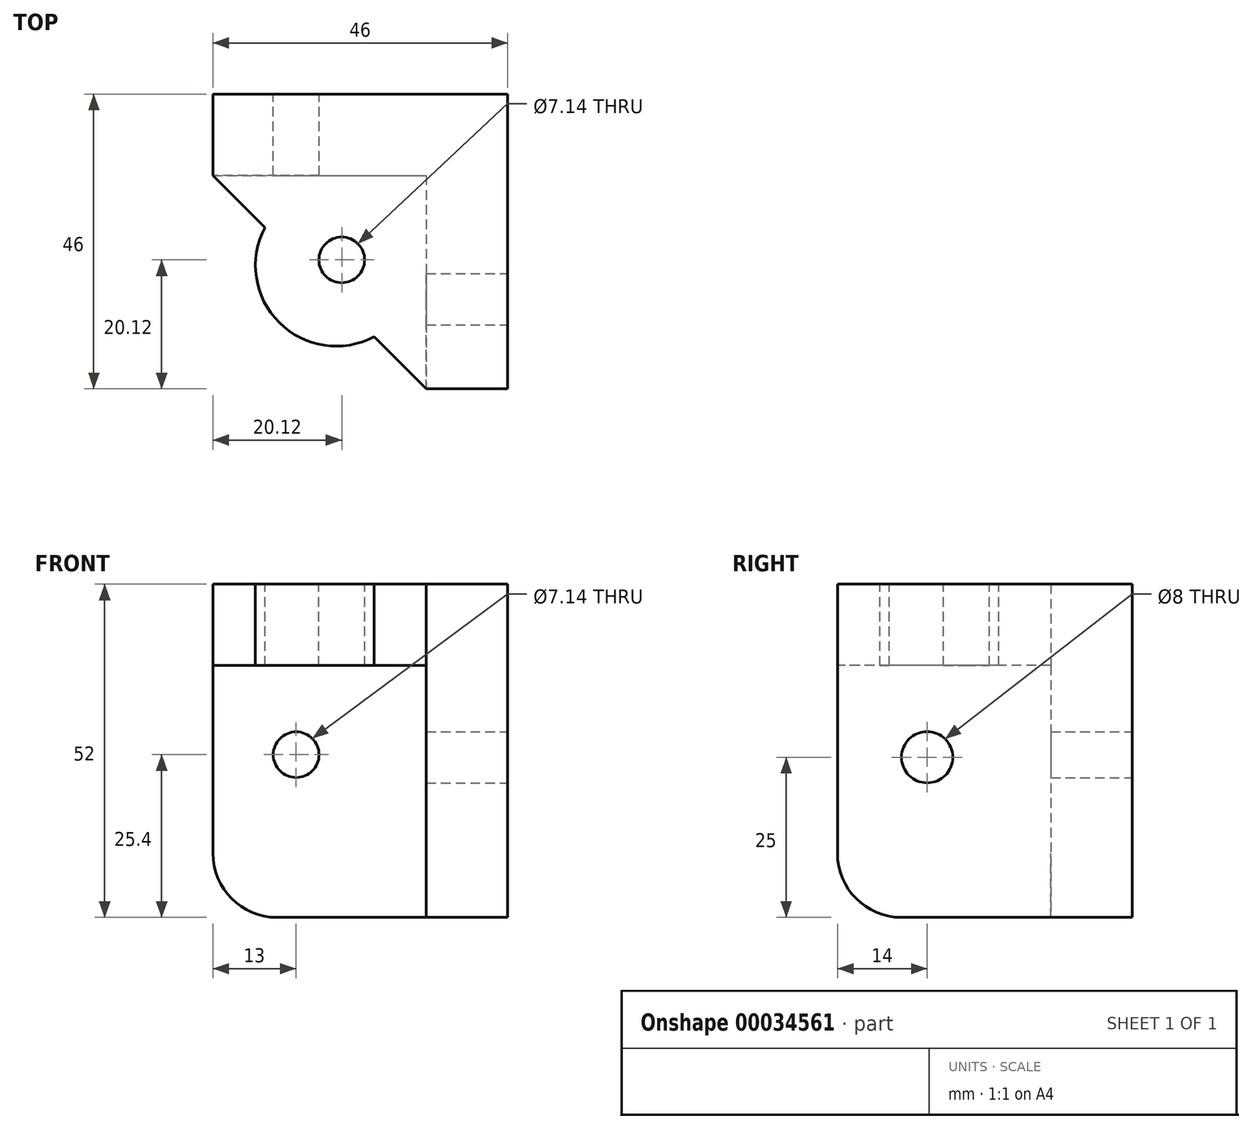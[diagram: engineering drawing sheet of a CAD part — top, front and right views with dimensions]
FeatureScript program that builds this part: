
annotation { "Feature Type Name" : "Feature", "Feature Type Description" : "" }
export const myFeature = defineFeature(function(context is Context, id is Id, definition is map)
    precondition{}
    {
        {
            var Q0;
            Q0=qCreatedBy(makeId("Top.planeOp"),FACE);
            var sketch = newSketch(context, id + "F0", { "sketchPlane" : qUnion([Q0])});
            skLineSegment(sketch, "E0.bottom", {"start": v(0, 0) * mm, "end": v(33.3, 0) * mm});
            skLineSegment(sketch, "E0.top", {"start": v(0, -12.7) * mm, "end": v(33.3, -12.7) * mm});
            skLineSegment(sketch, "E0.left", {"start": v(0, 0) * mm, "end": v(0, -12.7) * mm});
            skLineSegment(sketch, "E0.right", {"start": v(33.3, 0) * mm, "end": v(33.3, -12.7) * mm});
            skLineSegment(sketch, "E1.bottom", {"start": v(33.3, 0) * mm, "end": v(46, 0) * mm});
            skLineSegment(sketch, "E1.top", {"start": v(33.3, -46) * mm, "end": v(46, -46) * mm});
            skLineSegment(sketch, "E1.left", {"start": v(33.3, 0) * mm, "end": v(33.3, -46) * mm});
            skLineSegment(sketch, "E1.right", {"start": v(46, 0) * mm, "end": v(46, -46) * mm});
            skSolve(sketch);
        }
        {
            var Q0;
            Q0 = qSketchRegion(id + "F0", true);
            extrude(context, id + "F1", {"entities" : qUnion([Q0]), "depth" : 52 * mm});
        }
        {
            var Q0;
            Q0=makeQuery(id+"F1.opExtrude","CAP_FACE",FACE,{"disambiguationData":[OSD([sQuery(id+"F0.wireOp",EDGE,"E0.bottom"),sQuery(id+"F0.wireOp",EDGE,"E0.top"),sQuery(id+"F0.wireOp",EDGE,"E0.left"),sQuery(id+"F0.wireOp",EDGE,"E1.bottom"),sQuery(id+"F0.wireOp",EDGE,"E1.top"),sQuery(id+"F0.wireOp",EDGE,"E1.left"),sQuery(id+"F0.wireOp",EDGE,"E1.right")])],"isStart":false});
            var sketch = newSketch(context, id + "F2", { "sketchPlane" : qUnion([Q0])});
            skLineSegment(sketch, "E2.bottom", {"start": v(46, 0) * mm, "end": v(0, 0) * mm});
            skLineSegment(sketch, "E2.top", {"start": v(46, -46) * mm, "end": v(0, -46) * mm, "construction": true});
            skLineSegment(sketch, "E2.left", {"start": v(46, 0) * mm, "end": v(46, -46) * mm});
            skLineSegment(sketch, "E2.right", {"start": v(0, 0) * mm, "end": v(0, -46) * mm, "construction": true});
            skLineSegment(sketch, "E3", {"start": v(0, 0) * mm, "end": v(0, -12.7) * mm});
            skLineSegment(sketch, "E4", {"start": v(0, -12.7) * mm, "end": v(33.3, -46) * mm});
            skLineSegment(sketch, "E5", {"start": v(33.3, -46) * mm, "end": v(46, -46) * mm});
            skArc(sketch, "E6", {"start": v(8.13, -20.83) * mm, "mid": v(10.34, -35.66) * mm, "end": v(25.17, -37.87) * mm});
            skLineSegment(sketch, "E7", {"start": v(46, 0) * mm, "end": v(16.65, -29.35) * mm, "construction": true});
            skSolve(sketch);
        }
        {
            var Q0;
            Q0 = qSketchRegion(id + "F2", true);
            extrude(context, id + "F3", {"entities" : qUnion([Q0]), "operationType" : NewBodyOperationType.ADD, "oppositeDirection" : true, "depth" : 12.7 * mm});
        }
        {
            var Q0;
            Q0=makeQuery(id+"F1.opExtrude","SWEPT_FACE",FACE,{"disambiguationData":[OSD([sQuery(id+"F0.wireOp",EDGE,"E1.right")])]});
            var sketch = newSketch(context, id + "F4", { "sketchPlane" : qUnion([Q0])});
            skCircle(sketch, "E8", {"center": v(-32, 25) * mm, "radius": 4 * mm});
            skPoint(sketch, "E8.centerSnap0", {"position": v(-32, 0) * mm});
            skSolve(sketch);
        }
        {
            var Q0;
            Q0 = qSketchRegion(id + "F4", true);
            extrude(context, id + "F5", {"entities" : qUnion([Q0]), "operationType" : NewBodyOperationType.REMOVE, "endBound" : BoundingType.THROUGH_ALL, "oppositeDirection" : true, "depth" : 25 * mm});
        }
        {
            var Q0;
            Q0=makeQuery(id+"F1.opExtrude","SWEPT_FACE",FACE,{"disambiguationData":[OSD([sQuery(id+"F0.wireOp",EDGE,"E0.bottom"),sQuery(id+"F0.wireOp",EDGE,"E1.bottom")])]});
            var sketch = newSketch(context, id + "F6", { "sketchPlane" : qUnion([Q0])});
            skCircle(sketch, "E9", {"center": v(-13, 25.4) * mm, "radius": 3.57 * mm});
            skSolve(sketch);
        }
        {
            var Q0;
            Q0 = qSketchRegion(id + "F6", true);
            extrude(context, id + "F7", {"entities" : qUnion([Q0]), "operationType" : NewBodyOperationType.REMOVE, "oppositeDirection" : true, "depth" : 25 * mm});
        }
        {
            var Q0;
            Q0=makeQuery(id+"F3.boolean.opBoolean","MERGE",FACE,{"derivedFrom":[makeQuery(id+"F1.opExtrude","CAP_FACE",FACE,{"disambiguationData":[OSD([sQuery(id+"F0.wireOp",EDGE,"E0.bottom"),sQuery(id+"F0.wireOp",EDGE,"E0.top"),sQuery(id+"F0.wireOp",EDGE,"E0.left"),sQuery(id+"F0.wireOp",EDGE,"E1.bottom"),sQuery(id+"F0.wireOp",EDGE,"E1.top"),sQuery(id+"F0.wireOp",EDGE,"E1.left"),sQuery(id+"F0.wireOp",EDGE,"E1.right")])],"isStart":false}),makeQuery(id+"F3.opExtrude","CAP_FACE",FACE,{"disambiguationData":[OSD([sQuery(id+"F2.wireOp",EDGE,"E2.bottom"),sQuery(id+"F2.wireOp",EDGE,"E2.left"),sQuery(id+"F2.wireOp",EDGE,"E3"),sQuery(id+"F2.wireOp",EDGE,"E4"),sQuery(id+"F2.wireOp",EDGE,"E5"),sQuery(id+"F2.wireOp",EDGE,"E6")])],"isStart":true})]});
            var sketch = newSketch(context, id + "F8", { "sketchPlane" : qUnion([Q0])});
            skCircle(sketch, "E10", {"center": v(20.12, -25.88) * mm, "radius": 3.57 * mm});
            skLineSegment(sketch, "E11", {"start": v(46, 0) * mm, "end": v(10.34, -35.66) * mm, "construction": true});
            skSolve(sketch);
        }
        {
            var Q0;
            Q0 = qSketchRegion(id + "F8", true);
            extrude(context, id + "F9", {"entities" : qUnion([Q0]), "operationType" : NewBodyOperationType.REMOVE, "oppositeDirection" : true, "depth" : 25 * mm});
        }
        {
            var Q0;
            Q0=makeQuery(id+"F1.opExtrude","CAP_EDGE",EDGE,{"disambiguationData":[OSD([sQuery(id+"F0.wireOp",EDGE,"E1.top")])],"isStart":true});
            var Q1;
            Q1=makeQuery(id+"F1.opExtrude","CAP_EDGE",EDGE,{"disambiguationData":[OSD([sQuery(id+"F0.wireOp",EDGE,"E0.left")])],"isStart":true});
            fillet(context, id + "F10", {"entities" : qUnion([Q0, Q1]), "radius" : 10 * mm, "tangentPropagation" : true, "allowEdgeOverflow" : false});
        }
    });
